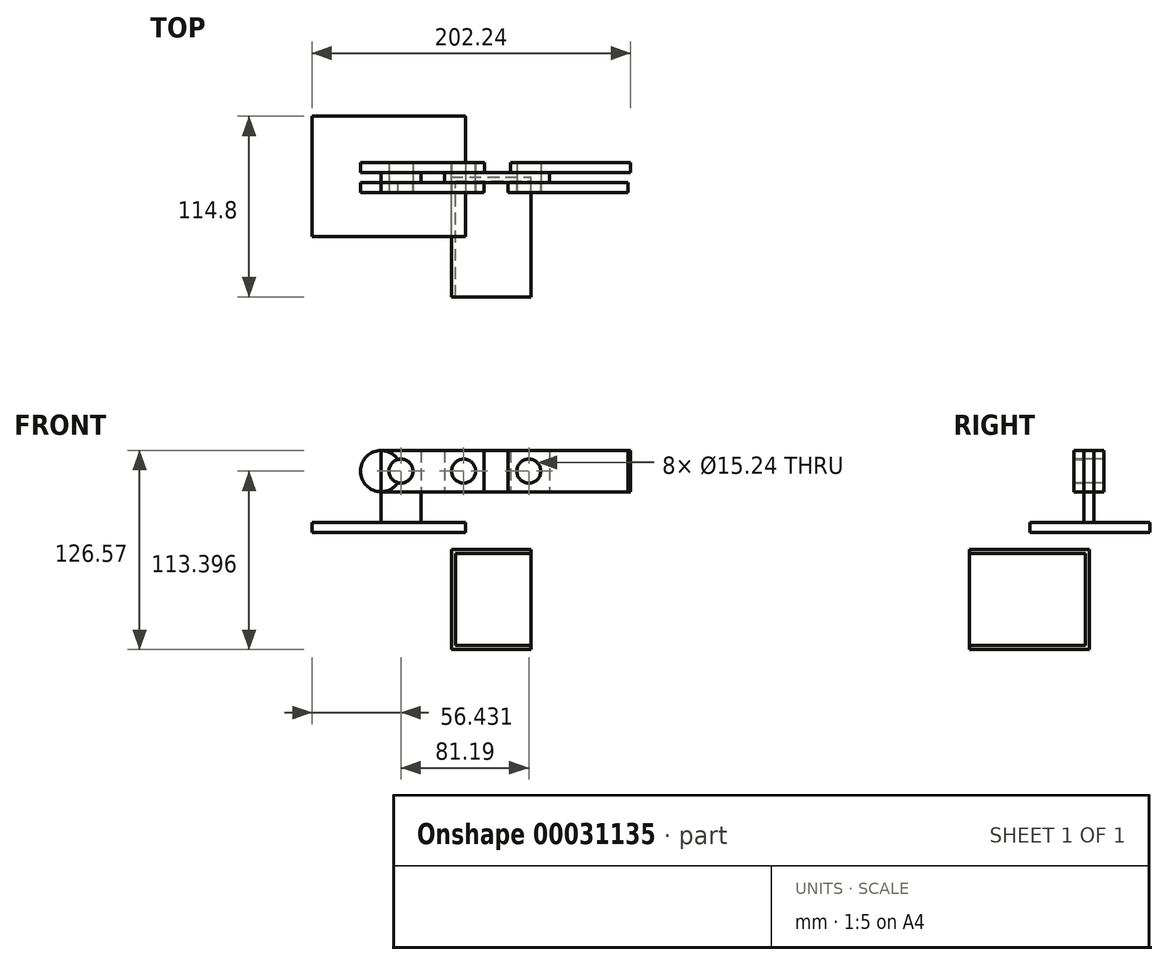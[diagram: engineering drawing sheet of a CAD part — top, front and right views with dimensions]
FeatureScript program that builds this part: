
annotation { "Feature Type Name" : "Feature", "Feature Type Description" : "" }
export const myFeature = defineFeature(function(context is Context, id is Id, definition is map)
    precondition{}
    {
        {
            var Q0;
            Q0=qCreatedBy(makeId("Top.planeOp"),FACE);
            var sketch = newSketch(context, id + "F0", { "sketchPlane" : qUnion([Q0])});
            skLineSegment(sketch, "E0.bottom", {"start": v(-48.08, 38.6) * mm, "end": v(49.48, 38.6) * mm});
            skLineSegment(sketch, "E0.top", {"start": v(-48.08, -37.9) * mm, "end": v(49.48, -37.9) * mm});
            skLineSegment(sketch, "E0.left", {"start": v(-48.08, 38.6) * mm, "end": v(-48.08, -37.9) * mm});
            skLineSegment(sketch, "E0.right", {"start": v(49.48, 38.6) * mm, "end": v(49.48, -37.9) * mm});
            skSolve(sketch);
        }
        {
            var Q0;
            Q0=makeQuery(id+"F0.imprint","IMPRINT",FACE,{"disambiguationData":[TD([[makeQuery(id+"F0.imprint","IMPRINT",EDGE,{"derivedFrom":sQuery(id+"F0.wireOp",EDGE,"E0.bottom")}),-1.0]])]});
            extrude(context, id + "F1", {"entities" : qUnion([Q0]), "oppositeDirection" : true, "depth" : 6.35 * mm});
        }
        {
            var Q0;
            Q0=makeQuery(id+"F1.opExtrude","CAP_FACE",FACE,{"disambiguationData":[OSD([sQuery(id+"F0.wireOp",EDGE,"E0.bottom"),sQuery(id+"F0.wireOp",EDGE,"E0.top"),sQuery(id+"F0.wireOp",EDGE,"E0.left"),sQuery(id+"F0.wireOp",EDGE,"E0.right")])],"isStart":true});
            var sketch = newSketch(context, id + "F2", { "sketchPlane" : qUnion([Q0])});
            skLineSegment(sketch, "E1.bottom", {"start": v(-4.35, 2.82) * mm, "end": v(21.05, 2.82) * mm});
            skLineSegment(sketch, "E1.top", {"start": v(-4.35, -3.53) * mm, "end": v(21.05, -3.53) * mm});
            skLineSegment(sketch, "E1.left", {"start": v(-4.35, 2.82) * mm, "end": v(-4.35, -3.53) * mm});
            skLineSegment(sketch, "E1.right", {"start": v(21.05, 2.82) * mm, "end": v(21.05, -3.53) * mm});
            skSolve(sketch);
        }
        {
            var Q0;
            Q0=makeQuery(id+"F2.imprint","IMPRINT",FACE,{"disambiguationData":[TD([[makeQuery(id+"F2.imprint","IMPRINT",EDGE,{"derivedFrom":sQuery(id+"F2.wireOp",EDGE,"E1.bottom")}),-1.0]])]});
            extrude(context, id + "F3", {"entities" : qUnion([Q0]), "operationType" : NewBodyOperationType.ADD, "depth" : 45.72 * mm});
        }
        {
            var Q0;
            Q0=makeQuery(id+"F3.opExtrude","SWEPT_FACE",FACE,{"disambiguationData":[OSD([sQuery(id+"F2.wireOp",EDGE,"E1.top")])]});
            var sketch = newSketch(context, id + "F4", { "sketchPlane" : qUnion([Q0])});
            skLineSegment(sketch, "E2", {"start": v(8.35, 45.72) * mm, "end": v(8.35, 32.64) * mm, "construction": true});
            skLineSegment(sketch, "E3", {"start": v(8.35, 32.64) * mm, "end": v(-4.35, 32.64) * mm, "construction": true});
            skCircle(sketch, "E4", {"center": v(8.35, 32.64) * mm, "radius": 7.62 * mm});
            skLineSegment(sketch, "E5.bottom", {"start": v(-4.35, 45.72) * mm, "end": v(21.05, 45.72) * mm});
            skLineSegment(sketch, "E5.top", {"start": v(-4.35, 19.55) * mm, "end": v(21.05, 19.55) * mm});
            skLineSegment(sketch, "E5.left", {"start": v(-4.35, 45.72) * mm, "end": v(-4.35, 19.55) * mm});
            skLineSegment(sketch, "E5.right", {"start": v(21.05, 45.72) * mm, "end": v(21.05, 19.55) * mm});
            skLineSegment(sketch, "E6.bottom", {"start": v(8.35, 32.64) * mm, "end": v(8.35, 32.64) * mm});
            skLineSegment(sketch, "E6.top", {"start": v(8.35, 19.55) * mm, "end": v(8.35, 19.55) * mm});
            skLineSegment(sketch, "E6.left", {"start": v(8.35, 32.64) * mm, "end": v(8.35, 19.55) * mm, "construction": true});
            skLineSegment(sketch, "E6.right", {"start": v(8.35, 32.64) * mm, "end": v(8.35, 19.55) * mm, "construction": true});
            skLineSegment(sketch, "E7.bottom", {"start": v(21.05, 45.72) * mm, "end": v(61.2, 45.72) * mm});
            skLineSegment(sketch, "E7.top", {"start": v(21.05, 19.55) * mm, "end": v(61.2, 19.55) * mm});
            skLineSegment(sketch, "E7.right", {"start": v(61.2, 45.72) * mm, "end": v(61.2, 19.55) * mm});
            skCircle(sketch, "E8", {"center": v(-4.35, 32.64) * mm, "radius": 13.08 * mm});
            skSolve(sketch);
        }
        {
            var Q0;
            {var subQ1=sQuery(id+"F4.wireOp",EDGE,"382f3984-db2c-4f21-befb-c2f1634ef591");var subQ3=sQuery(id+"F4.wireOp",EDGE,"E5.left");var subQ5=makeQuery(id+"F4.imprint","INTERSECT",VERTEX,{"derivedFrom":[subQ3,subQ1]});Q0=makeQuery(id+"F4.imprint","IMPRINT",FACE,{"disambiguationData":[TD([[makeQuery(id+"F4.imprint","IMPRINT",EDGE,{"disambiguationData":[TD([[subQ5,-1.0]])],"derivedFrom":subQ1}),1.0]])]});}
            var Q1;
            {var subQ0=sQuery(id+"F4.wireOp",EDGE,"382f3984-db2c-4f21-befb-c2f1634ef591");var subQ3=sQuery(id+"F4.wireOp",EDGE,"E4");var subQ5=makeQuery(id+"F4.imprint","INTERSECT",VERTEX,{"disambiguationData":[OD(0.0)],"derivedFrom":[subQ3,subQ0]});Q1=makeQuery(id+"F4.imprint","IMPRINT",FACE,{"disambiguationData":[TD([[makeQuery(id+"F4.imprint","IMPRINT",EDGE,{"disambiguationData":[TD([[subQ5,-1.0]])],"derivedFrom":subQ3}),-1.0]])]});}
            var Q2;
            {var subQ9=sQuery(id+"F4.wireOp",EDGE,"E5.bottom");Q2=makeQuery(id+"F4.imprint","IMPRINT",FACE,{"disambiguationData":[TD([[makeQuery(id+"F4.imprint","IMPRINT",EDGE,{"derivedFrom":subQ9}),-1.0]])]});}
            var Q3;
            Q3=makeQuery(id+"F4.imprint","IMPRINT",FACE,{"disambiguationData":[TD([[makeQuery(id+"F4.imprint","IMPRINT",EDGE,{"derivedFrom":sQuery(id+"F4.wireOp",EDGE,"E7.bottom")}),-1.0]])]});
            var Q4;
            {var subQ1=sQuery(id+"F4.wireOp",EDGE,"E5.left");Q4=makeQuery(id+"F4.imprint","IMPRINT",FACE,{"disambiguationData":[TD([[makeQuery(id+"F4.imprint","IMPRINT",EDGE,{"derivedFrom":subQ1}),-1.0]])]});}
            extrude(context, id + "F5", {"entities" : qUnion([Q0, Q1, Q2, Q3, Q4]), "depth" : 6.35 * mm});
        }
        {
            var Q0;
            {var subQ0=sQuery(id+"F4.wireOp",EDGE,"382f3984-db2c-4f21-befb-c2f1634ef591");var subQ1=sQuery(id+"F4.wireOp",EDGE,"E4");var subQ3=makeQuery(id+"F4.imprint","INTERSECT",VERTEX,{"disambiguationData":[OD(0.0)],"derivedFrom":[subQ1,subQ0]});Q0=makeQuery(id+"F4.imprint","IMPRINT",FACE,{"disambiguationData":[TD([[makeQuery(id+"F4.imprint","IMPRINT",EDGE,{"disambiguationData":[TD([[subQ3,-1.0]])],"derivedFrom":subQ1}),1.0]])]});}
            var Q1;
            {var subQ0=sQuery(id+"F4.wireOp",EDGE,"382f3984-db2c-4f21-befb-c2f1634ef591");var subQ1=sQuery(id+"F4.wireOp",EDGE,"E4");var subQ3=makeQuery(id+"F4.imprint","INTERSECT",VERTEX,{"disambiguationData":[OD(0.0)],"derivedFrom":[subQ1,subQ0]});Q1=makeQuery(id+"F4.imprint","IMPRINT",FACE,{"disambiguationData":[TD([[makeQuery(id+"F4.imprint","IMPRINT",EDGE,{"disambiguationData":[TD([[subQ3,1.0]])],"derivedFrom":subQ1}),1.0]])]});}
            extrude(context, id + "F6", {"entities" : qUnion([Q0, Q1]), "operationType" : NewBodyOperationType.REMOVE, "endBound" : BoundingType.THROUGH_ALL, "oppositeDirection" : true, "depth" : 7.04 * mm});
        }
        {
            var Q0;
            Q0=makeQuery(id+"F3.opExtrude","SWEPT_FACE",FACE,{"disambiguationData":[OSD([sQuery(id+"F2.wireOp",EDGE,"E1.bottom")])]});
            var sketch = newSketch(context, id + "F7", { "sketchPlane" : qUnion([Q0])});
            skCircle(sketch, "E9", {"center": v(-8.35, 32.64) * mm, "radius": 7.62 * mm});
            skLineSegment(sketch, "E10", {"start": v(-8.35, 45.72) * mm, "end": v(-8.35, 32.64) * mm, "construction": true});
            skLineSegment(sketch, "E11", {"start": v(4.35, 32.64) * mm, "end": v(-8.35, 32.64) * mm, "construction": true});
            skLineSegment(sketch, "E12.bottom", {"start": v(-61.3, 45.72) * mm, "end": v(4.35, 45.72) * mm});
            skLineSegment(sketch, "E12.top", {"start": v(-61.3, 19.55) * mm, "end": v(4.35, 19.55) * mm});
            skLineSegment(sketch, "E12.left", {"start": v(-61.3, 45.72) * mm, "end": v(-61.3, 19.55) * mm});
            skLineSegment(sketch, "E12.right", {"start": v(4.35, 45.72) * mm, "end": v(4.35, 19.55) * mm});
            skCircle(sketch, "E13", {"center": v(4.35, 32.64) * mm, "radius": 13.08 * mm});
            skSolve(sketch);
        }
        {
            var Q0;
            {var subQ1=sQuery(id+"F7.wireOp",EDGE,"E12.right");Q0=makeQuery(id+"F7.imprint","IMPRINT",FACE,{"disambiguationData":[TD([[makeQuery(id+"F7.imprint","IMPRINT",EDGE,{"derivedFrom":subQ1}),1.0]])]});}
            var Q1;
            {var subQ3=sQuery(id+"F7.wireOp",EDGE,"E12.right");Q1=makeQuery(id+"F7.imprint","IMPRINT",FACE,{"disambiguationData":[TD([[makeQuery(id+"F7.imprint","IMPRINT",EDGE,{"derivedFrom":subQ3}),-1.0]])]});}
            var Q2;
            {var subQ6=sQuery(id+"F7.wireOp",EDGE,"E13");var subQ7=sQuery(id+"F7.wireOp",EDGE,"E9");var subQ11=makeQuery(id+"F7.imprint","INTERSECT",VERTEX,{"disambiguationData":[OD(0.0)],"derivedFrom":[subQ7,subQ6]});Q2=makeQuery(id+"F7.imprint","IMPRINT",FACE,{"disambiguationData":[TD([[makeQuery(id+"F7.imprint","IMPRINT",EDGE,{"disambiguationData":[TD([[subQ11,-1.0]])],"derivedFrom":subQ7}),-1.0]])]});}
            var Q3;
            {var subQ5=sQuery(id+"F7.wireOp",EDGE,"E12.left");Q3=makeQuery(id+"F7.imprint","IMPRINT",FACE,{"disambiguationData":[TD([[makeQuery(id+"F7.imprint","IMPRINT",EDGE,{"derivedFrom":subQ5}),1.0]])]});}
            extrude(context, id + "F8", {"entities" : qUnion([Q0, Q1, Q2, Q3]), "depth" : 6.35 * mm});
        }
        {
            var Q0;
            Q0=makeQuery(id+"F5.opExtrude","CAP_FACE",FACE,{"disambiguationData":[OSD([sQuery(id+"F4.wireOp",EDGE,"E4"),sQuery(id+"F4.wireOp",EDGE,"E5.bottom"),sQuery(id+"F4.wireOp",EDGE,"E5.top"),sQuery(id+"F4.wireOp",EDGE,"E7.bottom"),sQuery(id+"F4.wireOp",EDGE,"E7.top"),sQuery(id+"F4.wireOp",EDGE,"E7.right"),sQuery(id+"F4.wireOp",EDGE,"E8")])],"isStart":false});
            var sketch = newSketch(context, id + "F9", { "sketchPlane" : qUnion([Q0])});
            skCircle(sketch, "E14", {"center": v(8.35, 32.64) * mm, "radius": 7.62 * mm});
            skSolve(sketch);
        }
        {
            var Q0;
            Q0=makeQuery(id+"F9.imprint","IMPRINT",FACE,{"disambiguationData":[TD([[makeQuery(id+"F9.imprint","IMPRINT",EDGE,{"derivedFrom":sQuery(id+"F9.wireOp",EDGE,"E14")}),1.0]])]});
            extrude(context, id + "F10", {"entities" : qUnion([Q0]), "oppositeDirection" : true, "depth" : 19.05 * mm});
        }
        {
            var Q0;
            Q0=makeQuery(id+"F5.opExtrude","CAP_FACE",FACE,{"disambiguationData":[OSD([sQuery(id+"F4.wireOp",EDGE,"E4"),sQuery(id+"F4.wireOp",EDGE,"E5.bottom"),sQuery(id+"F4.wireOp",EDGE,"E5.top"),sQuery(id+"F4.wireOp",EDGE,"E7.bottom"),sQuery(id+"F4.wireOp",EDGE,"E7.top"),sQuery(id+"F4.wireOp",EDGE,"E7.right"),sQuery(id+"F4.wireOp",EDGE,"E8")])],"isStart":false});
            var sketch = newSketch(context, id + "F11", { "sketchPlane" : qUnion([Q0])});
            skLineSegment(sketch, "E15", {"start": v(48.13, 45.72) * mm, "end": v(48.13, 19.55) * mm, "construction": true});
            skLineSegment(sketch, "E16", {"start": v(48.13, 19.55) * mm, "end": v(48.13, 32.64) * mm, "construction": true});
            skLineSegment(sketch, "E17", {"start": v(48.13, 32.64) * mm, "end": v(61.2, 32.64) * mm, "construction": true});
            skCircle(sketch, "E18", {"center": v(48.13, 32.64) * mm, "radius": 7.62 * mm});
            skSolve(sketch);
        }
        {
            var Q0;
            Q0=makeQuery(id+"F8.opExtrude","CAP_FACE",FACE,{"disambiguationData":[OSD([sQuery(id+"F7.wireOp",EDGE,"E9"),sQuery(id+"F7.wireOp",EDGE,"E12.bottom"),sQuery(id+"F7.wireOp",EDGE,"E12.top"),sQuery(id+"F7.wireOp",EDGE,"E12.left"),sQuery(id+"F7.wireOp",EDGE,"E13")])],"isStart":true});
            var sketch = newSketch(context, id + "F12", { "sketchPlane" : qUnion([Q0])});
            skLineSegment(sketch, "E19.bottom", {"start": v(36.14, 45.72) * mm, "end": v(102.62, 45.72) * mm});
            skLineSegment(sketch, "E19.top", {"start": v(36.14, 19.55) * mm, "end": v(102.62, 19.55) * mm});
            skLineSegment(sketch, "E19.left", {"start": v(36.14, 45.72) * mm, "end": v(36.14, 19.55) * mm});
            skLineSegment(sketch, "E19.right", {"start": v(102.62, 45.72) * mm, "end": v(102.62, 19.55) * mm});
            skCircle(sketch, "E20", {"center": v(48.13, 32.64) * mm, "radius": 7.62 * mm});
            skSolve(sketch);
        }
        {
            var Q0;
            {var subQ1=sQuery(id+"F12.wireOp",EDGE,"E19.right");Q0=makeQuery(id+"F12.imprint","IMPRINT",FACE,{"disambiguationData":[TD([[makeQuery(id+"F12.imprint","IMPRINT",EDGE,{"derivedFrom":subQ1}),-1.0]])]});}
            var Q1;
            {var subQ1=sQuery(id+"F12.wireOp",EDGE,"E19.left");Q1=makeQuery(id+"F12.imprint","IMPRINT",FACE,{"disambiguationData":[TD([[makeQuery(id+"F12.imprint","IMPRINT",EDGE,{"derivedFrom":subQ1}),1.0]])]});}
            extrude(context, id + "F13", {"entities" : qUnion([Q0, Q1]), "depth" : 6.35 * mm});
        }
        {
            var Q0;
            Q0=makeQuery(id+"F13.opExtrude","CAP_FACE",FACE,{"disambiguationData":[OSD([sQuery(id+"F12.wireOp",EDGE,"E19.bottom"),sQuery(id+"F12.wireOp",EDGE,"E19.top"),sQuery(id+"F12.wireOp",EDGE,"E19.left"),sQuery(id+"F12.wireOp",EDGE,"E19.right"),sQuery(id+"F12.wireOp",EDGE,"E20")])],"isStart":false});
            var sketch = newSketch(context, id + "F14", { "sketchPlane" : qUnion([Q0])});
            skLineSegment(sketch, "E21", {"start": v(89.54, 45.72) * mm, "end": v(89.54, 19.55) * mm, "construction": true});
            skLineSegment(sketch, "E22", {"start": v(89.54, 19.55) * mm, "end": v(89.54, 32.64) * mm, "construction": true});
            skLineSegment(sketch, "E23", {"start": v(89.54, 32.64) * mm, "end": v(102.62, 32.64) * mm, "construction": true});
            skCircle(sketch, "E24", {"center": v(89.54, 32.64) * mm, "radius": 7.62 * mm});
            skSolve(sketch);
        }
        {
            var Q0;
            Q0=makeQuery(id+"F14.imprint","IMPRINT",FACE,{"disambiguationData":[TD([[makeQuery(id+"F14.imprint","IMPRINT",EDGE,{"derivedFrom":sQuery(id+"F14.wireOp",EDGE,"E24")}),1.0]])]});
            extrude(context, id + "F15", {"entities" : qUnion([Q0]), "operationType" : NewBodyOperationType.REMOVE, "endBound" : BoundingType.THROUGH_ALL, "oppositeDirection" : true, "depth" : 25.4 * mm});
        }
        {
            var Q0;
            Q0=makeQuery(id+"F8.opExtrude","CAP_FACE",FACE,{"disambiguationData":[OSD([sQuery(id+"F7.wireOp",EDGE,"E9"),sQuery(id+"F7.wireOp",EDGE,"E12.bottom"),sQuery(id+"F7.wireOp",EDGE,"E12.top"),sQuery(id+"F7.wireOp",EDGE,"E12.left"),sQuery(id+"F7.wireOp",EDGE,"E13")])],"isStart":false});
            var sketch = newSketch(context, id + "F16", { "sketchPlane" : qUnion([Q0])});
            skCircle(sketch, "E25", {"center": v(-48.13, 32.64) * mm, "radius": 7.62 * mm});
            skSolve(sketch);
        }
        {
            var Q0;
            Q0=makeQuery(id+"F16.imprint","IMPRINT",FACE,{"disambiguationData":[TD([[makeQuery(id+"F16.imprint","IMPRINT",EDGE,{"derivedFrom":sQuery(id+"F16.wireOp",EDGE,"E25")}),1.0]])]});
            extrude(context, id + "F17", {"entities" : qUnion([Q0]), "operationType" : NewBodyOperationType.REMOVE, "endBound" : BoundingType.THROUGH_ALL, "oppositeDirection" : true, "depth" : 25.4 * mm});
        }
        {
            var Q0;
            Q0=makeQuery(id+"F11.imprint","IMPRINT",FACE,{"disambiguationData":[TD([[makeQuery(id+"F11.imprint","IMPRINT",EDGE,{"derivedFrom":sQuery(id+"F11.wireOp",EDGE,"E18")}),1.0]])]});
            extrude(context, id + "F18", {"entities" : qUnion([Q0]), "operationType" : NewBodyOperationType.REMOVE, "endBound" : BoundingType.THROUGH_ALL, "oppositeDirection" : true, "depth" : 19.05 * mm});
        }
        {
            var Q0;
            Q0=makeQuery(id+"F5.opExtrude","CAP_FACE",FACE,{"disambiguationData":[OSD([sQuery(id+"F4.wireOp",EDGE,"E4"),sQuery(id+"F4.wireOp",EDGE,"E5.bottom"),sQuery(id+"F4.wireOp",EDGE,"E5.top"),sQuery(id+"F4.wireOp",EDGE,"E7.bottom"),sQuery(id+"F4.wireOp",EDGE,"E7.top"),sQuery(id+"F4.wireOp",EDGE,"E7.right"),sQuery(id+"F4.wireOp",EDGE,"E8")])],"isStart":false});
            var sketch = newSketch(context, id + "F19", { "sketchPlane" : qUnion([Q0])});
            skCircle(sketch, "E26", {"center": v(48.13, 32.64) * mm, "radius": 7.62 * mm});
            skSolve(sketch);
        }
        {
            var Q0;
            Q0=makeQuery(id+"F19.imprint","IMPRINT",FACE,{"disambiguationData":[TD([[makeQuery(id+"F19.imprint","IMPRINT",EDGE,{"derivedFrom":sQuery(id+"F19.wireOp",EDGE,"E26")}),1.0]])]});
            extrude(context, id + "F20", {"entities" : qUnion([Q0]), "oppositeDirection" : true, "depth" : 19.05 * mm});
        }
        {
            var Q0;
            Q0=makeQuery(id+"F13.opExtrude","CAP_FACE",FACE,{"disambiguationData":[OSD([sQuery(id+"F12.wireOp",EDGE,"E19.bottom"),sQuery(id+"F12.wireOp",EDGE,"E19.top"),sQuery(id+"F12.wireOp",EDGE,"E19.left"),sQuery(id+"F12.wireOp",EDGE,"E19.right"),sQuery(id+"F12.wireOp",EDGE,"E20")])],"isStart":false});
            var sketch = newSketch(context, id + "F21", { "sketchPlane" : qUnion([Q0])});
            skCircle(sketch, "E27", {"center": v(89.54, 32.64) * mm, "radius": 7.62 * mm});
            skLineSegment(sketch, "E28.bottom", {"start": v(76.45, 45.72) * mm, "end": v(152.65, 45.72) * mm});
            skLineSegment(sketch, "E28.top", {"start": v(76.45, 19.55) * mm, "end": v(152.65, 19.55) * mm});
            skLineSegment(sketch, "E28.left", {"start": v(76.45, 45.72) * mm, "end": v(76.45, 19.55) * mm});
            skLineSegment(sketch, "E28.right", {"start": v(152.65, 45.72) * mm, "end": v(152.65, 19.55) * mm});
            skLineSegment(sketch, "E29", {"start": v(76.45, 32.64) * mm, "end": v(102.62, 32.64) * mm});
            skLineSegment(sketch, "E30", {"start": v(89.54, 45.72) * mm, "end": v(89.54, 19.55) * mm});
            skSolve(sketch);
        }
        {
            var Q0;
            {var subQ1=sQuery(id+"F21.wireOp",EDGE,"E28.right");Q0=makeQuery(id+"F21.imprint","IMPRINT",FACE,{"disambiguationData":[TD([[makeQuery(id+"F21.imprint","IMPRINT",EDGE,{"derivedFrom":subQ1}),-1.0]])]});}
            var Q1;
            Q1=makeQuery(id+"F21.imprint","IMPRINT",FACE,{"disambiguationData":[TD([[makeQuery(id+"F21.imprint","IMPRINT",EDGE,{"derivedFrom":sQuery(id+"F21.wireOp",EDGE,"E27")}),-1.0]])]});
            extrude(context, id + "F22", {"entities" : qUnion([Q0, Q1]), "depth" : 6.35 * mm});
        }
        {
            var Q0;
            Q0=makeQuery(id+"F13.opExtrude","CAP_FACE",FACE,{"disambiguationData":[OSD([sQuery(id+"F12.wireOp",EDGE,"E19.bottom"),sQuery(id+"F12.wireOp",EDGE,"E19.top"),sQuery(id+"F12.wireOp",EDGE,"E19.left"),sQuery(id+"F12.wireOp",EDGE,"E19.right"),sQuery(id+"F12.wireOp",EDGE,"E20")])],"isStart":true});
            var sketch = newSketch(context, id + "F23", { "sketchPlane" : qUnion([Q0])});
            skCircle(sketch, "E31", {"center": v(-89.54, 32.64) * mm, "radius": 7.62 * mm});
            skLineSegment(sketch, "E32.bottom", {"start": v(-154.16, 45.8) * mm, "end": v(-77.96, 45.8) * mm});
            skLineSegment(sketch, "E32.top", {"start": v(-154.16, 19.55) * mm, "end": v(-77.96, 19.55) * mm});
            skLineSegment(sketch, "E32.left", {"start": v(-154.16, 45.8) * mm, "end": v(-154.16, 19.55) * mm});
            skLineSegment(sketch, "E32.right", {"start": v(-77.96, 45.8) * mm, "end": v(-77.96, 19.55) * mm});
            skSolve(sketch);
        }
        {
            var Q0;
            Q0=makeQuery(id+"F23.imprint","IMPRINT",FACE,{"disambiguationData":[TD([[makeQuery(id+"F23.imprint","IMPRINT",EDGE,{"derivedFrom":sQuery(id+"F23.wireOp",EDGE,"E31")}),1.0]])]});
            var Q1;
            {var subQ4=sQuery(id+"F23.wireOp",EDGE,"E32.bottom");Q1=makeQuery(id+"F23.imprint","IMPRINT",FACE,{"disambiguationData":[TD([[makeQuery(id+"F23.imprint","IMPRINT",EDGE,{"derivedFrom":subQ4}),-1.0]])]});}
            extrude(context, id + "F24", {"entities" : qUnion([Q0, Q1]), "depth" : 6.35 * mm});
        }
        {
            var Q0;
            Q0=makeQuery(id+"F22.opExtrude","CAP_FACE",FACE,{"disambiguationData":[OSD([sQuery(id+"F21.wireOp",EDGE,"E27"),sQuery(id+"F21.wireOp",EDGE,"E28.bottom"),sQuery(id+"F21.wireOp",EDGE,"E28.top"),sQuery(id+"F21.wireOp",EDGE,"E28.left"),sQuery(id+"F21.wireOp",EDGE,"E28.right")])],"isStart":false});
            var sketch = newSketch(context, id + "F25", { "sketchPlane" : qUnion([Q0])});
            skCircle(sketch, "E33", {"center": v(89.54, 32.64) * mm, "radius": 7.62 * mm});
            skSolve(sketch);
        }
        {
            var Q0;
            Q0=makeQuery(id+"F25.imprint","IMPRINT",FACE,{"disambiguationData":[TD([[makeQuery(id+"F25.imprint","IMPRINT",EDGE,{"derivedFrom":sQuery(id+"F25.wireOp",EDGE,"E33")}),1.0]])]});
            extrude(context, id + "F26", {"entities" : qUnion([Q0]), "oppositeDirection" : true, "depth" : 19.05 * mm});
        }
        {
            var Q0;
            Q0=qCreatedBy(makeId("Front.planeOp"),FACE);
            var sketch = newSketch(context, id + "F27", { "sketchPlane" : qUnion([Q0])});
            skLineSegment(sketch, "E34.bottom", {"start": v(40.31, -17.26) * mm, "end": v(91.11, -17.26) * mm});
            skLineSegment(sketch, "E34.top", {"start": v(40.31, -80.76) * mm, "end": v(91.11, -80.76) * mm});
            skLineSegment(sketch, "E34.left", {"start": v(40.31, -17.26) * mm, "end": v(40.31, -80.76) * mm});
            skLineSegment(sketch, "E34.right", {"start": v(91.11, -17.26) * mm, "end": v(91.11, -80.76) * mm});
            skSolve(sketch);
        }
        {
            var Q0;
            Q0=makeQuery(id+"F27.imprint","IMPRINT",FACE,{"disambiguationData":[TD([[makeQuery(id+"F27.imprint","IMPRINT",EDGE,{"derivedFrom":sQuery(id+"F27.wireOp",EDGE,"E34.bottom")}),-1.0]])]});
            extrude(context, id + "F28", {"entities" : qUnion([Q0]), "depth" : 76.2 * mm});
        }
        {
            var Q0;
            Q0=makeQuery(id+"F28.opExtrude","CAP_FACE",FACE,{"disambiguationData":[OSD([sQuery(id+"F27.wireOp",EDGE,"E34.bottom"),sQuery(id+"F27.wireOp",EDGE,"E34.top"),sQuery(id+"F27.wireOp",EDGE,"E34.left"),sQuery(id+"F27.wireOp",EDGE,"E34.right")])],"isStart":false});
            shell(context, id + "F29", {"entities" : qUnion([Q0]), "thickness" : 2.54 * mm});
        }
        {
            var Q0;
            Q0=makeQuery(id+"F28.opExtrude","SWEPT_FACE",FACE,{"disambiguationData":[OSD([sQuery(id+"F27.wireOp",EDGE,"E34.right")])]});
            var sketch = newSketch(context, id + "F30", { "sketchPlane" : qUnion([Q0])});
            skLineSegment(sketch, "E35.bottom", {"start": v(-76.2, -19.8) * mm, "end": v(-2.54, -19.8) * mm});
            skLineSegment(sketch, "E35.top", {"start": v(-76.2, -78.22) * mm, "end": v(-2.54, -78.22) * mm});
            skLineSegment(sketch, "E35.left", {"start": v(-76.2, -19.8) * mm, "end": v(-76.2, -78.22) * mm});
            skLineSegment(sketch, "E35.right", {"start": v(-2.54, -19.8) * mm, "end": v(-2.54, -78.22) * mm});
            skSolve(sketch);
        }
        {
            var Q0;
            Q0=makeQuery(id+"F30.imprint","IMPRINT",FACE,{"disambiguationData":[TD([[makeQuery(id+"F30.imprint","IMPRINT",EDGE,{"derivedFrom":sQuery(id+"F30.wireOp",EDGE,"E35.bottom")}),-1.0]])]});
            extrude(context, id + "F31", {"entities" : qUnion([Q0]), "operationType" : NewBodyOperationType.REMOVE, "oppositeDirection" : true, "depth" : 25.4 * mm});
        }
    });
